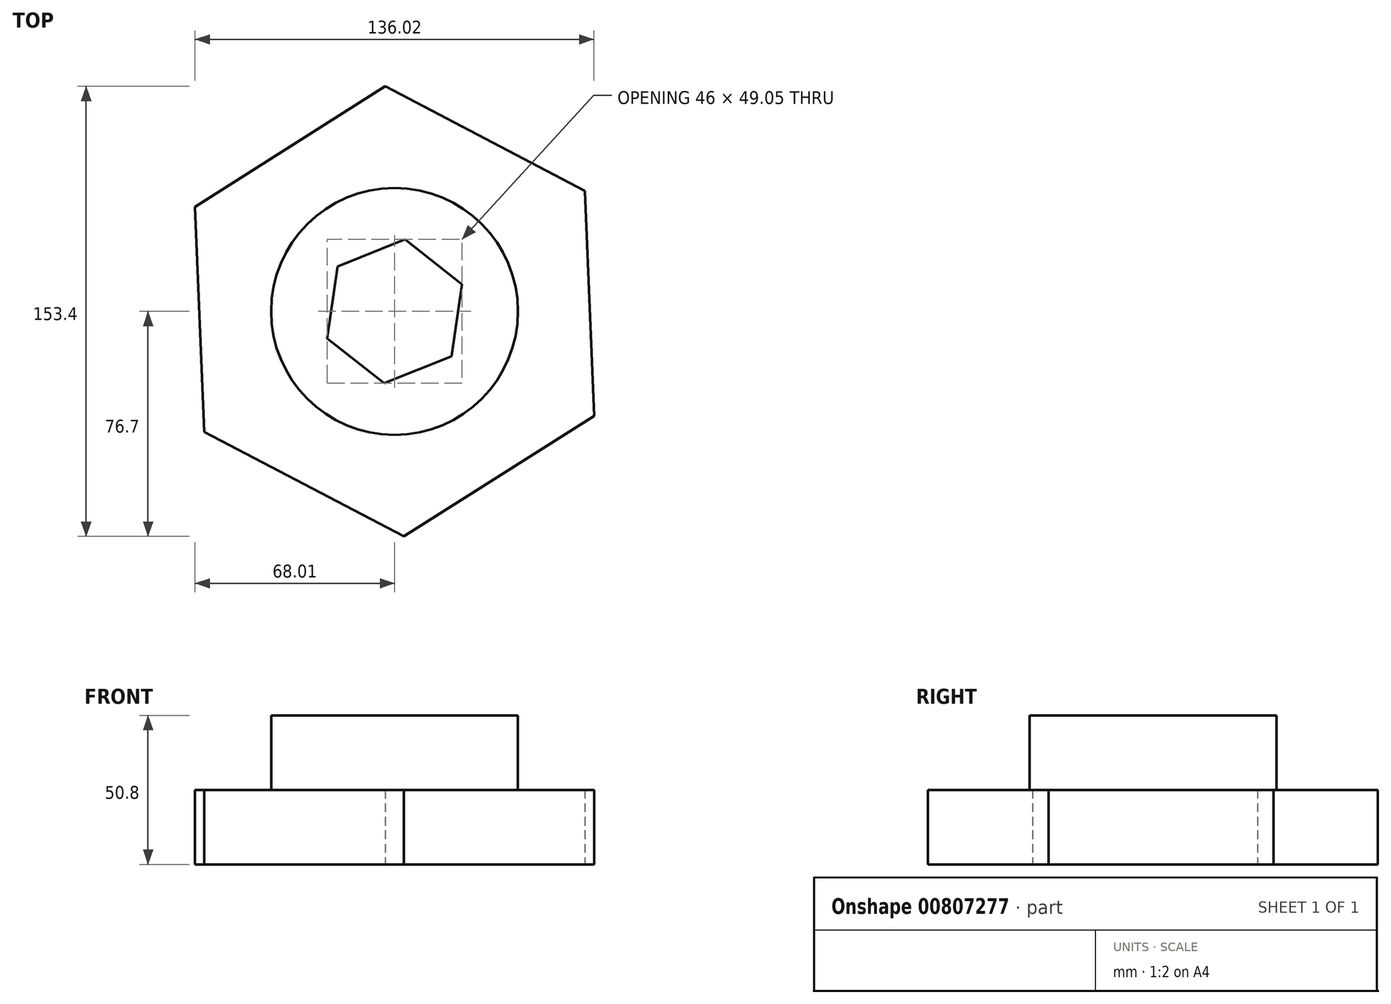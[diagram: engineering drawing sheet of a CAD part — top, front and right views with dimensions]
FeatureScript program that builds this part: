
annotation { "Feature Type Name" : "Feature", "Feature Type Description" : "" }
export const myFeature = defineFeature(function(context is Context, id is Id, definition is map)
    precondition{}
    {
        {
            var Q0;
            Q0=qCreatedBy(makeId("Top.planeOp"),FACE);
            var sketch = newSketch(context, id + "F0", { "sketchPlane" : qUnion([Q0])});
            skCircle(sketch, "E0.cCircle", {"center": v(0, 0) * mm, "radius": 66.48 * mm, "construction": true});
            skLineSegment(sketch, "E0.0", {"start": v(-68.01, 35.6) * mm, "end": v(-3.17, 76.7) * mm});
            skLineSegment(sketch, "E0.1", {"start": v(-3.17, 76.7) * mm, "end": v(64.84, 41.1) * mm});
            skLineSegment(sketch, "E0.2", {"start": v(64.84, 41.1) * mm, "end": v(68.01, -35.6) * mm});
            skLineSegment(sketch, "E0.3", {"start": v(68.01, -35.6) * mm, "end": v(3.17, -76.7) * mm});
            skLineSegment(sketch, "E0.4", {"start": v(3.17, -76.7) * mm, "end": v(-64.84, -41.1) * mm});
            skLineSegment(sketch, "E0.5", {"start": v(-64.84, -41.1) * mm, "end": v(-68.01, 35.6) * mm});
            skPoint(sketch, "E0.0.midPoint", {"position": v(-35.6, 56.15) * mm});
            skSolve(sketch);
        }
        {
            var Q0;
            Q0=makeQuery(id+"F0.imprint","IMPRINT",FACE,{"disambiguationData":[TD([[makeQuery(id+"F0.imprint","IMPRINT",EDGE,{"derivedFrom":sQuery(id+"F0.wireOp",EDGE,"E0.0")}),-1.0]])]});
            extrude(context, id + "F1", {"entities" : qUnion([Q0]), "depth" : 25.4 * mm, "offsetDistance" : 25.4 * mm});
        }
        {
            var Q0;
            Q0=makeQuery(id+"F1.opExtrude","CAP_FACE",FACE,{"disambiguationData":[OSD([sQuery(id+"F0.wireOp",EDGE,"E0.0"),sQuery(id+"F0.wireOp",EDGE,"E0.1"),sQuery(id+"F0.wireOp",EDGE,"E0.2"),sQuery(id+"F0.wireOp",EDGE,"E0.3"),sQuery(id+"F0.wireOp",EDGE,"E0.4"),sQuery(id+"F0.wireOp",EDGE,"E0.5")])],"isStart":false});
            var sketch = newSketch(context, id + "F2", { "sketchPlane" : qUnion([Q0])});
            skCircle(sketch, "E1", {"center": v(0, 0) * mm, "radius": 42.08 * mm});
            skSolve(sketch);
        }
        {
            var Q0;
            Q0=makeQuery(id+"F2.imprint","IMPRINT",FACE,{"disambiguationData":[TD([[makeQuery(id+"F2.imprint","IMPRINT",EDGE,{"derivedFrom":sQuery(id+"F2.wireOp",EDGE,"E1")}),1.0]])]});
            extrude(context, id + "F3", {"entities" : qUnion([Q0]), "operationType" : NewBodyOperationType.ADD, "depth" : 25.4 * mm, "offsetDistance" : 25.4 * mm});
        }
        {
            var Q0;
            Q0=makeQuery(id+"F3.opExtrude","CAP_FACE",FACE,{"disambiguationData":[OSD([sQuery(id+"F2.wireOp",EDGE,"E1")])],"isStart":false});
            var sketch = newSketch(context, id + "F4", { "sketchPlane" : qUnion([Q0])});
            skCircle(sketch, "E2.cCircle", {"center": v(0, 0) * mm, "radius": 21.46 * mm, "construction": true});
            skLineSegment(sketch, "E2.0", {"start": v(-19.48, 15.3) * mm, "end": v(3.52, 24.52) * mm});
            skLineSegment(sketch, "E2.1", {"start": v(3.52, 24.52) * mm, "end": v(23, 9.21) * mm});
            skLineSegment(sketch, "E2.2", {"start": v(23, 9.21) * mm, "end": v(19.48, -15.3) * mm});
            skLineSegment(sketch, "E2.3", {"start": v(19.48, -15.3) * mm, "end": v(-3.52, -24.52) * mm});
            skLineSegment(sketch, "E2.4", {"start": v(-3.52, -24.52) * mm, "end": v(-23, -9.21) * mm});
            skLineSegment(sketch, "E2.5", {"start": v(-23, -9.21) * mm, "end": v(-19.48, 15.3) * mm});
            skPoint(sketch, "E2.0.midPoint", {"position": v(-7.98, 19.92) * mm});
            skSolve(sketch);
        }
        {
            var Q0;
            Q0 = qSketchRegion(id + "F4", true);
            extrude(context, id + "F5", {"entities" : qUnion([Q0]), "operationType" : NewBodyOperationType.REMOVE, "endBound" : BoundingType.UP_TO_NEXT, "oppositeDirection" : true, "depth" : 25.4 * mm, "offsetDistance" : 25.4 * mm});
        }
    });
